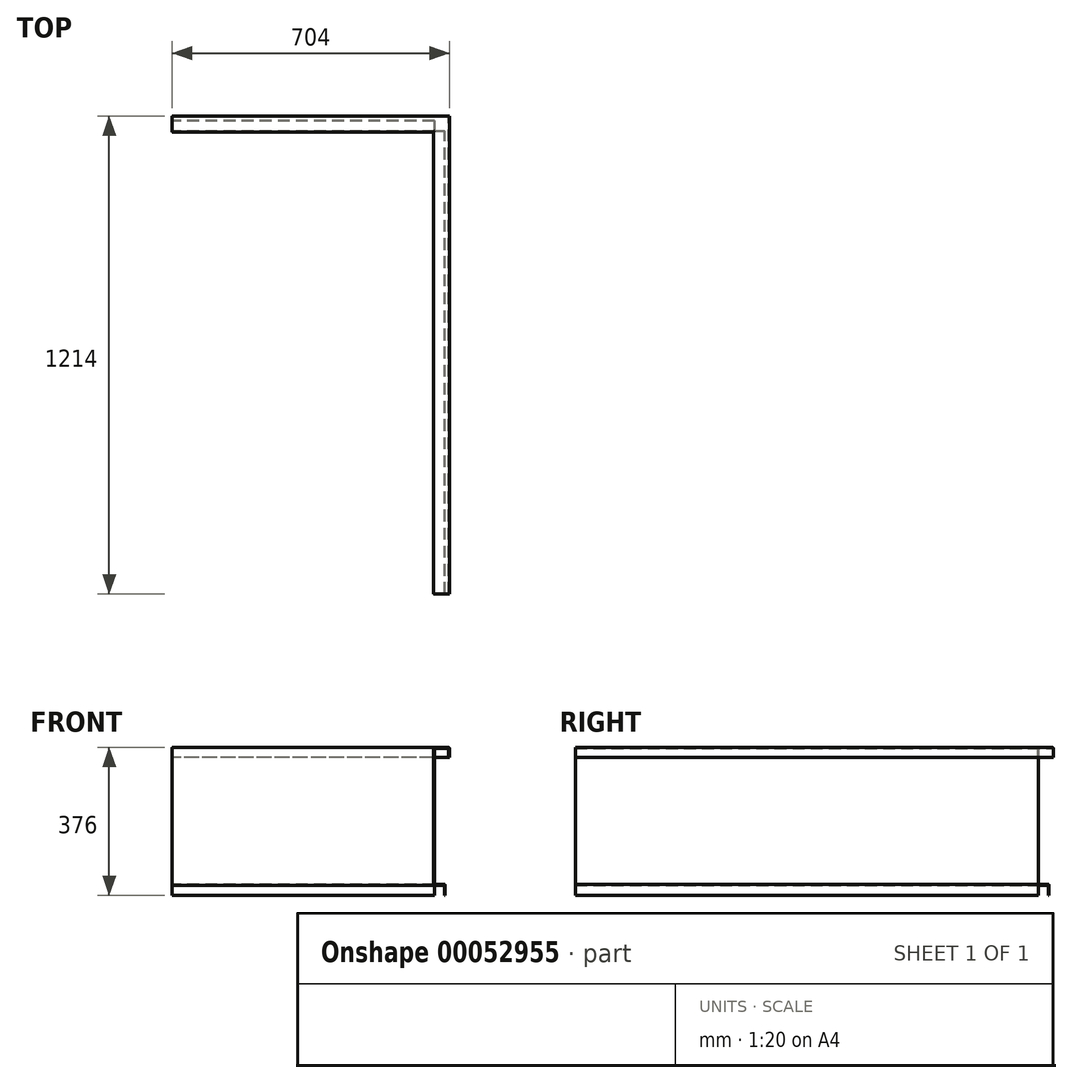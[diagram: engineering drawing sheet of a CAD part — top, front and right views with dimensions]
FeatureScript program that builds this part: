
annotation { "Feature Type Name" : "Feature", "Feature Type Description" : "" }
export const myFeature = defineFeature(function(context is Context, id is Id, definition is map)
    precondition{}
    {
        {
            var Q0;
            Q0=qCreatedBy(makeId("Front.planeOp"),FACE);
            var sketch = newSketch(context, id + "F0", { "sketchPlane" : qUnion([Q0])});
            skLineSegment(sketch, "E0", {"start": v(38, -25) * mm, "end": v(38, -2) * mm});
            skLineSegment(sketch, "E1", {"start": v(38, -2) * mm, "end": v(2, -2) * mm});
            skLineSegment(sketch, "E2", {"start": v(2, -2) * mm, "end": v(2, -348) * mm});
            skLineSegment(sketch, "E3", {"start": v(2, -348) * mm, "end": v(29, -348) * mm});
            skLineSegment(sketch, "E4", {"start": v(29, -348) * mm, "end": v(29, -376) * mm});
            skLineSegment(sketch, "E5.0", {"start": v(27, -350) * mm, "end": v(27, -376) * mm});
            skLineSegment(sketch, "E5.1", {"start": v(40, -25) * mm, "end": v(40, 0) * mm});
            skLineSegment(sketch, "E5.2", {"start": v(40, 0) * mm, "end": v(0, 0) * mm});
            skLineSegment(sketch, "E5.3", {"start": v(0, 0) * mm, "end": v(0, -350) * mm});
            skLineSegment(sketch, "E5.4", {"start": v(0, -350) * mm, "end": v(27, -350) * mm});
            skLineSegment(sketch, "E6", {"start": v(27, -376) * mm, "end": v(29, -376) * mm});
            skLineSegment(sketch, "E7", {"start": v(38, -25) * mm, "end": v(40, -25) * mm});
            skSolve(sketch);
        }
        {
            var Q0;
            Q0=qCreatedBy(makeId("Top.planeOp"),FACE);
            var sketch = newSketch(context, id + "F1", { "sketchPlane" : qUnion([Q0])});
            skLineSegment(sketch, "E8", {"start": v(0, 0) * mm, "end": v(0, 1174) * mm});
            skLineSegment(sketch, "E9", {"start": v(0, 1174) * mm, "end": v(-664, 1174) * mm});
            skSolve(sketch);
        }
        {
            var Q0;
            Q0 = qSketchRegion(id + "F0", true);
            var Q1;
            Q1 = qConstructionFilter(qBodyType(qCreatedBy(id + "F1" ,EDGE), BodyType.WIRE), ConstructionObject.NO);
            sweep(context, id + "F2", {"profiles" : qUnion([Q0]), "path" : qUnion([Q1])});
        }
        {
            var Q0;
            Q0=makeQuery(id+"F2.opSweep","SWEPT_FACE",FACE,{"disambiguationData":[OSD([sQuery(id+"F0.wireOp",EDGE,"E3"),sQuery(id+"F1.wireOp",EDGE,"E8")])]});
            var sketch = newSketch(context, id + "F3", { "sketchPlane" : qUnion([Q0])});
            skLineSegment(sketch, "E10", {"start": v(2, 1176) * mm, "end": v(2, 1203) * mm});
            skLineSegment(sketch, "E11", {"start": v(2, 1203) * mm, "end": v(29, 1203) * mm});
            skLineSegment(sketch, "E12", {"start": v(29, 1203) * mm, "end": v(29, 1176) * mm});
            skLineSegment(sketch, "E13", {"start": v(29, 1176) * mm, "end": v(2, 1176) * mm});
            skSolve(sketch);
        }
        {
            var Q0;
            Q0 = qSketchRegion(id + "F3", true);
            extrude(context, id + "F4", {"entities" : qUnion([Q0]), "operationType" : NewBodyOperationType.REMOVE, "oppositeDirection" : true, "depth" : 30 * mm});
        }
        {
            var Q0;
            Q0=makeQuery(id+"F2.opSweep","SWEPT_EDGE",EDGE,{"disambiguationData":[OSD([sQuery(id+"F0.wireOp",EDGE,"E5.0"),sQuery(id+"F0.wireOp",EDGE,"E5.4"),sQuery(id+"F1.wireOp",EDGE,"E9")])]});
            var Q1;
            Q1=makeQuery(id+"F2.opSweep","SWEPT_EDGE",EDGE,{"disambiguationData":[OSD([sQuery(id+"F0.wireOp",EDGE,"E5.3"),sQuery(id+"F0.wireOp",EDGE,"E5.4"),sQuery(id+"F1.wireOp",EDGE,"E9")])]});
            var Q2;
            Q2=makeQuery(id+"F2.opSweep","SWEPT_EDGE",EDGE,{"disambiguationData":[OSD([sQuery(id+"F0.wireOp",EDGE,"E3"),sQuery(id+"F0.wireOp",EDGE,"E4"),sQuery(id+"F1.wireOp",EDGE,"E9")])]});
            var Q3;
            Q3=makeQuery(id+"F2.opSweep","SWEPT_EDGE",EDGE,{"disambiguationData":[OSD([sQuery(id+"F0.wireOp",EDGE,"E2"),sQuery(id+"F0.wireOp",EDGE,"E3"),sQuery(id+"F1.wireOp",EDGE,"E9")])]});
            var Q4;
            Q4=makeQuery(id+"F2.opSweep","SWEPT_EDGE",EDGE,{"disambiguationData":[OSD([sQuery(id+"F0.wireOp",EDGE,"E5.2"),sQuery(id+"F0.wireOp",EDGE,"E5.3"),sQuery(id+"F1.wireOp",EDGE,"E9")])]});
            var Q5;
            Q5=makeQuery(id+"F2.opSweep","SWEPT_EDGE",EDGE,{"disambiguationData":[OSD([sQuery(id+"F0.wireOp",EDGE,"E5.1"),sQuery(id+"F0.wireOp",EDGE,"E5.2"),sQuery(id+"F1.wireOp",EDGE,"E9")])]});
            var Q6;
            Q6=makeQuery(id+"F2.opSweep","SWEPT_EDGE",EDGE,{"disambiguationData":[OSD([sQuery(id+"F0.wireOp",EDGE,"E1"),sQuery(id+"F0.wireOp",EDGE,"E2"),sQuery(id+"F1.wireOp",EDGE,"E9")])]});
            var Q7;
            Q7=makeQuery(id+"F2.opSweep","SWEPT_EDGE",EDGE,{"disambiguationData":[OSD([sQuery(id+"F0.wireOp",EDGE,"E0"),sQuery(id+"F0.wireOp",EDGE,"E1"),sQuery(id+"F1.wireOp",EDGE,"E9")])]});
            var Q8;
            Q8=makeQuery(id+"F2.opSweep","SWEPT_EDGE",EDGE,{"disambiguationData":[OSD([sQuery(id+"F0.wireOp",EDGE,"E5.1"),sQuery(id+"F0.wireOp",EDGE,"E5.2"),sQuery(id+"F1.wireOp",EDGE,"E8")])]});
            var Q9;
            Q9=makeQuery(id+"F2.opSweep","SWEPT_EDGE",EDGE,{"disambiguationData":[OSD([sQuery(id+"F0.wireOp",EDGE,"E5.2"),sQuery(id+"F0.wireOp",EDGE,"E5.3"),sQuery(id+"F1.wireOp",EDGE,"E8")])]});
            var Q10;
            Q10=makeQuery(id+"F2.opSweep","SWEPT_EDGE",EDGE,{"disambiguationData":[OSD([sQuery(id+"F0.wireOp",EDGE,"E5.3"),sQuery(id+"F0.wireOp",EDGE,"E5.4"),sQuery(id+"F1.wireOp",EDGE,"E8")])]});
            var Q11;
            Q11=makeQuery(id+"F2.opSweep","SWEPT_EDGE",EDGE,{"disambiguationData":[OSD([sQuery(id+"F0.wireOp",EDGE,"E5.0"),sQuery(id+"F0.wireOp",EDGE,"E5.4"),sQuery(id+"F1.wireOp",EDGE,"E8")])]});
            var Q12;
            Q12=makeQuery(id+"F2.opSweep","SWEPT_EDGE",EDGE,{"disambiguationData":[OSD([sQuery(id+"F0.wireOp",EDGE,"E0"),sQuery(id+"F0.wireOp",EDGE,"E1"),sQuery(id+"F1.wireOp",EDGE,"E8")])]});
            var Q13;
            Q13=makeQuery(id+"F2.opSweep","SWEPT_EDGE",EDGE,{"disambiguationData":[OSD([sQuery(id+"F0.wireOp",EDGE,"E1"),sQuery(id+"F0.wireOp",EDGE,"E2"),sQuery(id+"F1.wireOp",EDGE,"E8")])]});
            var Q14;
            Q14=makeQuery(id+"F2.opSweep","SWEPT_EDGE",EDGE,{"disambiguationData":[OSD([sQuery(id+"F0.wireOp",EDGE,"E3"),sQuery(id+"F0.wireOp",EDGE,"E4"),sQuery(id+"F1.wireOp",EDGE,"E8")])]});
            fillet(context, id + "F5", {"entities" : qUnion([Q0, Q1, Q2, Q3, Q4, Q5, Q6, Q7, Q8, Q9, Q10, Q11, Q12, Q13, Q14]), "radius" : 2 * mm, "tangentPropagation" : true, "allowEdgeOverflow" : false});
        }
    });
